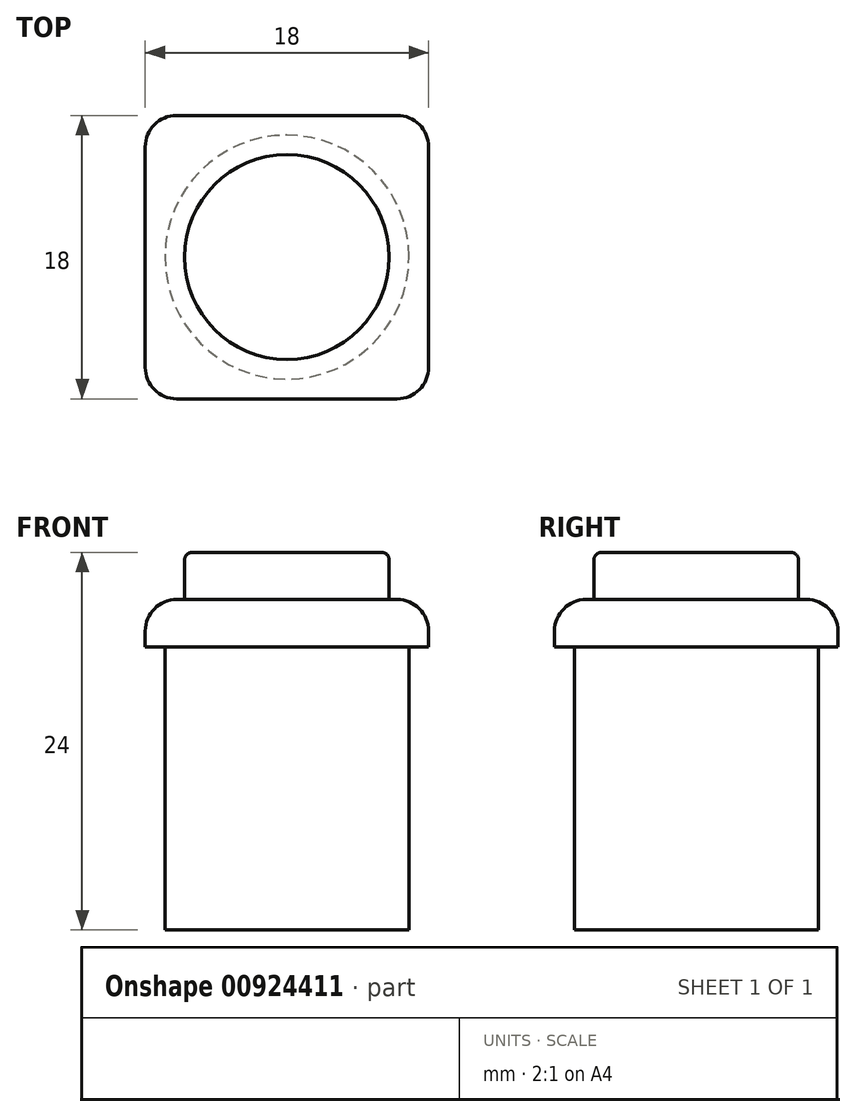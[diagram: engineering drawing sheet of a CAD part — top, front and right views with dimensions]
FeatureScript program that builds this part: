
annotation { "Feature Type Name" : "Feature", "Feature Type Description" : "" }
export const myFeature = defineFeature(function(context is Context, id is Id, definition is map)
    precondition{}
    {
        {
            var Q0;
            Q0=qCreatedBy(makeId("Top.planeOp"),FACE);
            var sketch = newSketch(context, id + "F0", { "sketchPlane" : qUnion([Q0])});
            skLineSegment(sketch, "E0.bottom", {"start": v(9, -9) * mm, "end": v(-9, -9) * mm});
            skLineSegment(sketch, "E0.top", {"start": v(9, 9) * mm, "end": v(-9, 9) * mm});
            skLineSegment(sketch, "E0.left", {"start": v(9, -9) * mm, "end": v(9, 9) * mm});
            skLineSegment(sketch, "E0.right", {"start": v(-9, -9) * mm, "end": v(-9, 9) * mm});
            skPoint(sketch, "E0.middle", {"position": v(0, 0) * mm});
            skSolve(sketch);
        }
        {
            var Q0;
            Q0 = qSketchRegion(id + "F0", true);
            extrude(context, id + "F1", {"entities" : qUnion([Q0]), "depth" : 3 * mm, "offsetDistance" : 25 * mm});
        }
        {
            var Q0;
            Q0=makeQuery(id+"F1.opExtrude","CAP_FACE",FACE,{"disambiguationData":[OSD([sQuery(id+"F0.wireOp",EDGE,"E0.bottom"),sQuery(id+"F0.wireOp",EDGE,"E0.top"),sQuery(id+"F0.wireOp",EDGE,"E0.left"),sQuery(id+"F0.wireOp",EDGE,"E0.right")])],"isStart":false});
            var sketch = newSketch(context, id + "F2", { "sketchPlane" : qUnion([Q0])});
            skCircle(sketch, "E1", {"center": v(0, 0) * mm, "radius": 6.5 * mm});
            skSolve(sketch);
        }
        {
            var Q0;
            Q0=makeQuery(id+"F2.imprint","IMPRINT",FACE,{"disambiguationData":[TD([[makeQuery(id+"F2.imprint","IMPRINT",EDGE,{"derivedFrom":sQuery(id+"F2.wireOp",EDGE,"E1")}),1.0]])]});
            extrude(context, id + "F3", {"entities" : qUnion([Q0]), "operationType" : NewBodyOperationType.ADD, "depth" : 3 * mm, "offsetDistance" : 25 * mm});
        }
        {
            var Q0;
            Q0=makeQuery(id+"F1.opExtrude","CAP_EDGE",EDGE,{"disambiguationData":[OSD([sQuery(id+"F0.wireOp",EDGE,"E0.left")])],"isStart":false});
            var Q1;
            Q1=makeQuery(id+"F1.opExtrude","CAP_EDGE",EDGE,{"disambiguationData":[OSD([sQuery(id+"F0.wireOp",EDGE,"E0.top")])],"isStart":false});
            var Q2;
            Q2=makeQuery(id+"F1.opExtrude","CAP_EDGE",EDGE,{"disambiguationData":[OSD([sQuery(id+"F0.wireOp",EDGE,"E0.right")])],"isStart":false});
            var Q3;
            Q3=makeQuery(id+"F1.opExtrude","CAP_EDGE",EDGE,{"disambiguationData":[OSD([sQuery(id+"F0.wireOp",EDGE,"E0.bottom")])],"isStart":false});
            var Q4;
            Q4=makeQuery(id+"F1.opExtrude","SWEPT_EDGE",EDGE,{"disambiguationData":[OSD([sQuery(id+"F0.wireOp",EDGE,"E0.bottom"),sQuery(id+"F0.wireOp",EDGE,"E0.right")])]});
            var Q5;
            Q5=makeQuery(id+"F1.opExtrude","SWEPT_EDGE",EDGE,{"disambiguationData":[OSD([sQuery(id+"F0.wireOp",EDGE,"E0.top"),sQuery(id+"F0.wireOp",EDGE,"E0.right")])]});
            var Q6;
            Q6=makeQuery(id+"F1.opExtrude","SWEPT_EDGE",EDGE,{"disambiguationData":[OSD([sQuery(id+"F0.wireOp",EDGE,"E0.bottom"),sQuery(id+"F0.wireOp",EDGE,"E0.left")])]});
            var Q7;
            Q7=makeQuery(id+"F1.opExtrude","SWEPT_EDGE",EDGE,{"disambiguationData":[OSD([sQuery(id+"F0.wireOp",EDGE,"E0.top"),sQuery(id+"F0.wireOp",EDGE,"E0.left")])]});
            fillet(context, id + "F4", {"entities" : qUnion([Q0, Q1, Q2, Q3, Q4, Q5, Q6, Q7]), "radius" : 2 * mm, "tangentPropagation" : true, "allowEdgeOverflow" : false});
        }
        {
            var Q0;
            Q0=makeQuery(id+"F3.opExtrude","CAP_EDGE",EDGE,{"disambiguationData":[OSD([sQuery(id+"F2.wireOp",EDGE,"E1")])],"isStart":false});
            fillet(context, id + "F5", {"entities" : qUnion([Q0]), "radius" : 0.5 * mm, "tangentPropagation" : true, "allowEdgeOverflow" : false});
        }
        {
            var Q0;
            Q0=makeQuery(id+"F1.opExtrude","CAP_FACE",FACE,{"disambiguationData":[OSD([sQuery(id+"F0.wireOp",EDGE,"E0.bottom"),sQuery(id+"F0.wireOp",EDGE,"E0.top"),sQuery(id+"F0.wireOp",EDGE,"E0.left"),sQuery(id+"F0.wireOp",EDGE,"E0.right")])],"isStart":true});
            var sketch = newSketch(context, id + "F6", { "sketchPlane" : qUnion([Q0])});
            skCircle(sketch, "E2", {"center": v(0, 0) * mm, "radius": 7.75 * mm});
            skSolve(sketch);
        }
        {
            var Q0;
            Q0=makeQuery(id+"F6.imprint","IMPRINT",FACE,{"disambiguationData":[TD([[makeQuery(id+"F6.imprint","IMPRINT",EDGE,{"derivedFrom":sQuery(id+"F6.wireOp",EDGE,"E2")}),1.0]])]});
            extrude(context, id + "F7", {"entities" : qUnion([Q0]), "operationType" : NewBodyOperationType.ADD, "depth" : 18 * mm, "offsetDistance" : 25 * mm});
        }
    });
